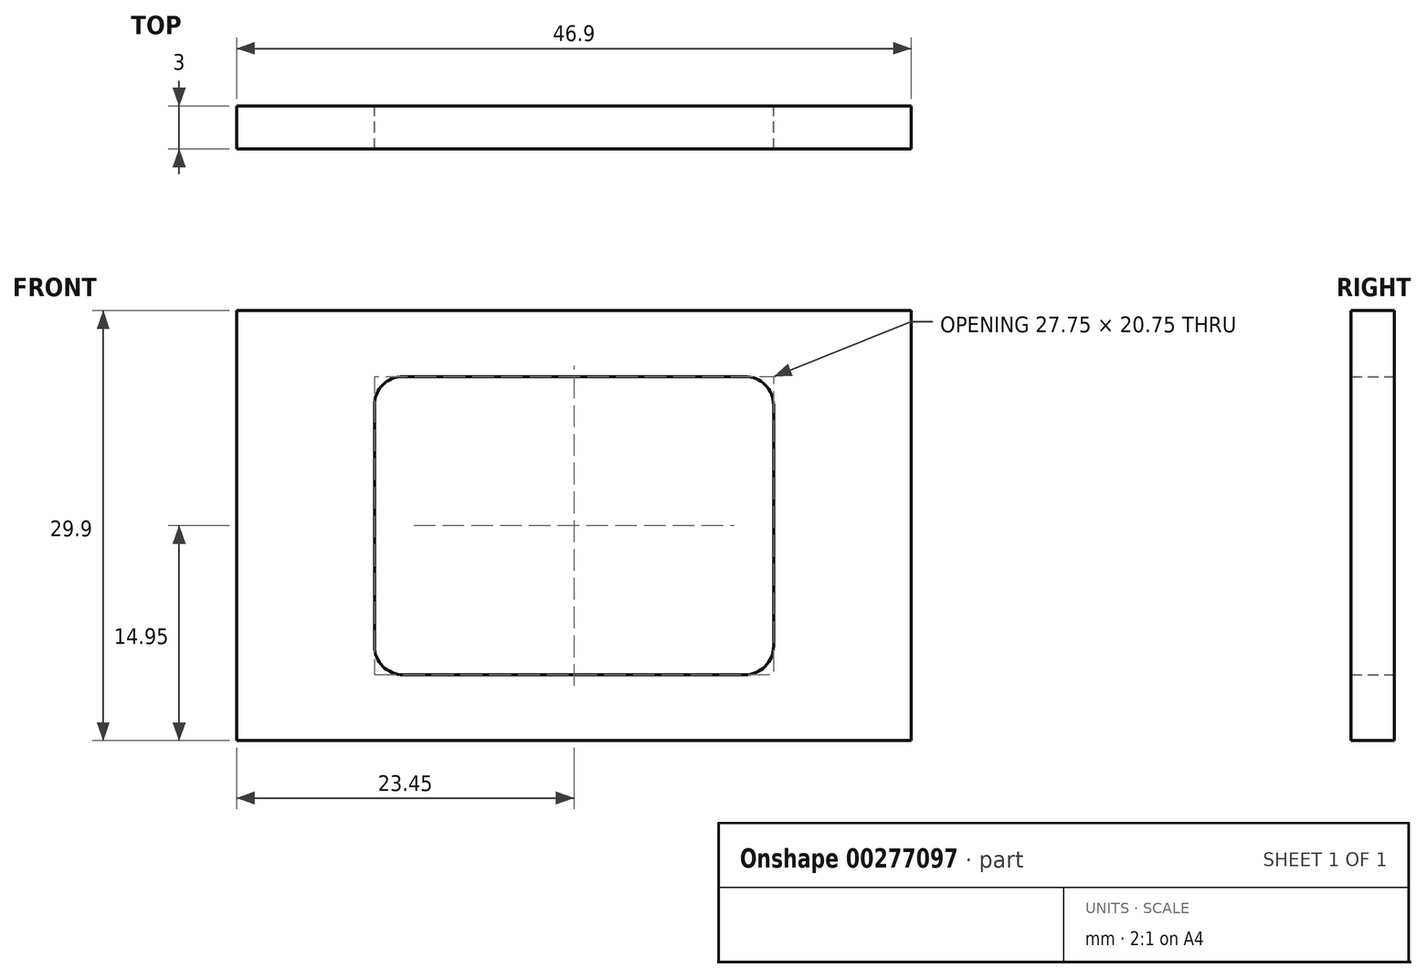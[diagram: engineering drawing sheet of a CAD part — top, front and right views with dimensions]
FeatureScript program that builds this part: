
annotation { "Feature Type Name" : "Feature", "Feature Type Description" : "" }
export const myFeature = defineFeature(function(context is Context, id is Id, definition is map)
    precondition{}
    {
        {
            var Q0;
            Q0=qCreatedBy(makeId("Front.planeOp"),FACE);
            var sketch = newSketch(context, id + "F0", { "sketchPlane" : qUnion([Q0])});
            skLineSegment(sketch, "E0.bottom", {"start": v(23.45, -14.95) * mm, "end": v(-23.45, -14.95) * mm});
            skLineSegment(sketch, "E0.top", {"start": v(23.45, 14.95) * mm, "end": v(-23.45, 14.95) * mm});
            skLineSegment(sketch, "E0.left", {"start": v(23.45, -14.95) * mm, "end": v(23.45, 14.95) * mm});
            skLineSegment(sketch, "E0.right", {"start": v(-23.45, -14.95) * mm, "end": v(-23.45, 14.95) * mm});
            skPoint(sketch, "E0.middle", {"position": v(0, 0) * mm});
            skLineSegment(sketch, "E1.bottom", {"start": v(-11.87, -10.37) * mm, "end": v(11.88, -10.37) * mm});
            skLineSegment(sketch, "E1.top", {"start": v(-11.88, 10.37) * mm, "end": v(11.88, 10.37) * mm});
            skLineSegment(sketch, "E1.left", {"start": v(-13.87, -8.37) * mm, "end": v(-13.88, 8.37) * mm});
            skLineSegment(sketch, "E1.right", {"start": v(13.88, -8.37) * mm, "end": v(13.88, 8.38) * mm});
            skPoint(sketch, "E2.visualSharp", {"position": v(-13.88, 10.37) * mm});
            skArc(sketch, "E2.filletArc", {"start": v(-11.88, 10.37) * mm, "mid": v(-13.29, 9.79) * mm, "end": v(-13.88, 8.37) * mm});
            skPoint(sketch, "E3.visualSharp", {"position": v(-13.87, -10.37) * mm});
            skArc(sketch, "E3.filletArc", {"start": v(-13.87, -8.37) * mm, "mid": v(-13.29, -9.79) * mm, "end": v(-11.87, -10.37) * mm});
            skPoint(sketch, "E4.visualSharp", {"position": v(13.88, -10.37) * mm});
            skArc(sketch, "E4.filletArc", {"start": v(11.88, -10.37) * mm, "mid": v(13.29, -9.79) * mm, "end": v(13.88, -8.37) * mm});
            skPoint(sketch, "E5.visualSharp", {"position": v(13.87, 10.37) * mm});
            skArc(sketch, "E5.filletArc", {"start": v(13.88, 8.38) * mm, "mid": v(13.29, 9.79) * mm, "end": v(11.88, 10.37) * mm});
            skSolve(sketch);
        }
        {
            var Q0;
            Q0=makeQuery(id+"F0.imprint","IMPRINT",FACE,{"disambiguationData":[TD([[makeQuery(id+"F0.imprint","IMPRINT",EDGE,{"derivedFrom":sQuery(id+"F0.wireOp",EDGE,"E0.bottom")}),-1.0]])]});
            extrude(context, id + "F1", {"entities" : qUnion([Q0]), "depth" : 3 * mm});
        }
    });
